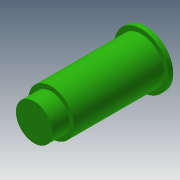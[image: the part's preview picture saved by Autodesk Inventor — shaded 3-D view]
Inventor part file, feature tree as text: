
AUTODESK INVENTOR PART (.ipt)
format: ipt  version: 2014 (Build 180170000, 170)  size: 98,816 bytes
history: native  units: mm
features: revolve x1, sketch x1
ambient origin geometry x8: Origin, YZ Plane, XZ Plane, XY Plane, X Axis, Y Axis, Z Axis, Center Point
bodies: Solid1 (feature_tree)
feature tree (2):
  revolve  "Revolution1"  [1 undecoded]
  sketch  "Sketch1"  dims[d0=9.0mm d1=1.5mm d2=29.7mm d3=5.6mm d4=7.5mm d5=6.0mm d6=90.0deg]
note: 1 required parameter value undecoded (feature->parameter linkage not recoverable at this tier; creation-order binding heuristic only, values carry confidence <= 0.55)
